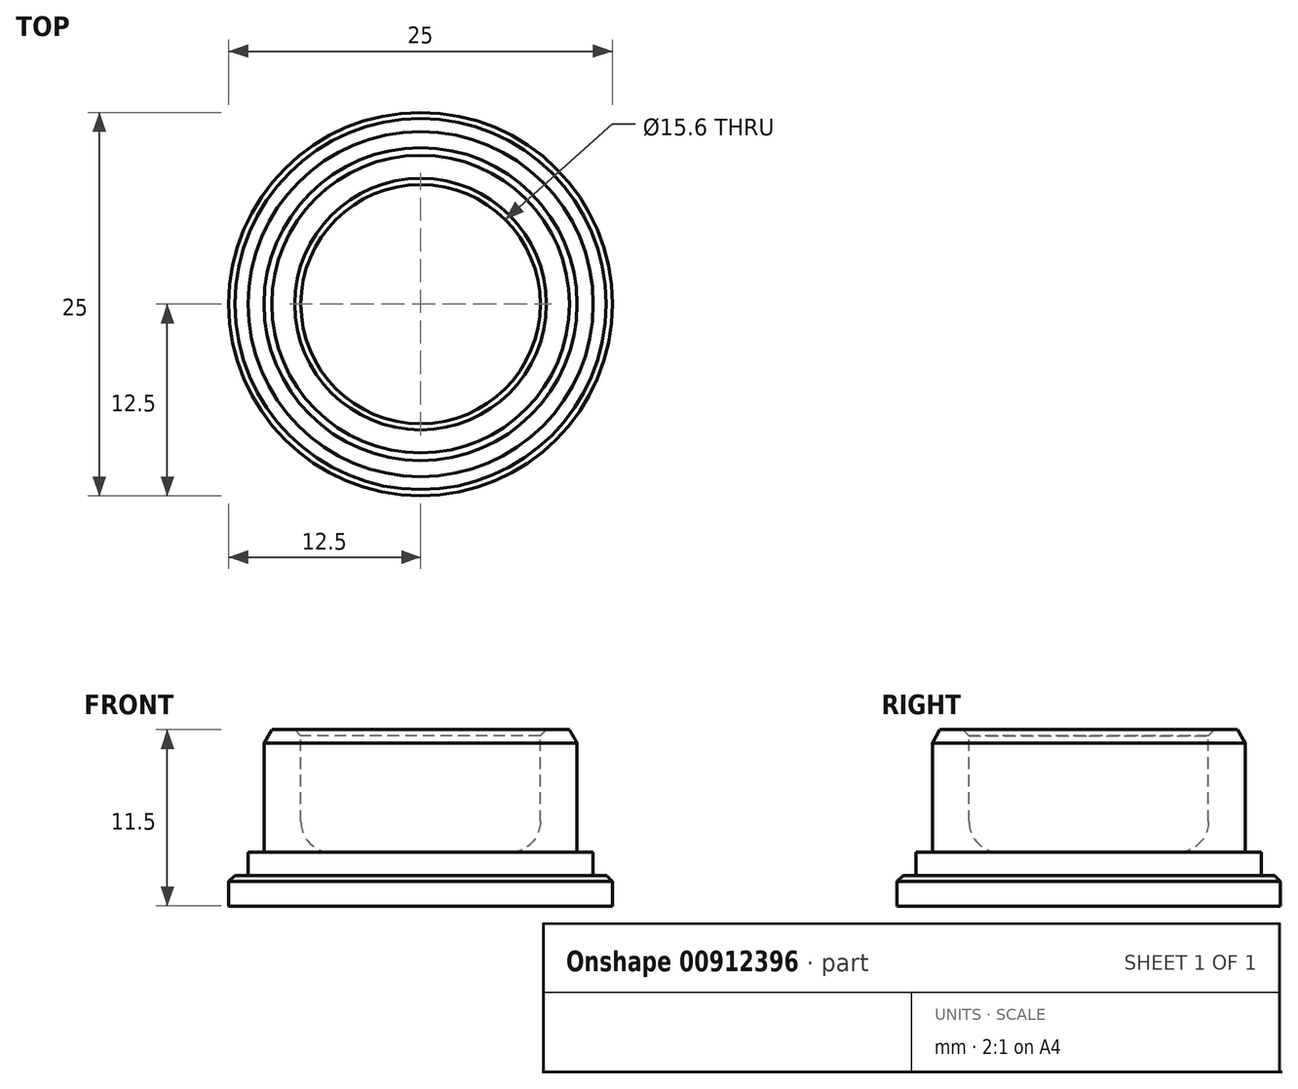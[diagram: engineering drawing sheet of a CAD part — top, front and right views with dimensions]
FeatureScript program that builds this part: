
annotation { "Feature Type Name" : "Feature", "Feature Type Description" : "" }
export const myFeature = defineFeature(function(context is Context, id is Id, definition is map)
    precondition{}
    {
        {
            var Q0;
            Q0=qCreatedBy(makeId("Front.planeOp"),FACE);
            var sketch = newSketch(context, id + "F0", { "sketchPlane" : qUnion([Q0])});
            skLineSegment(sketch, "E0", {"start": v(0, 14.43) * mm, "end": v(0, -11.95) * mm, "construction": true});
            skLineSegment(sketch, "E1", {"start": v(7.8, 5.82) * mm, "end": v(7.8, -2.18) * mm});
            skLineSegment(sketch, "E2", {"start": v(7.8, -2.18) * mm, "end": v(0, -2.18) * mm});
            skLineSegment(sketch, "E3", {"start": v(7.8, 5.82) * mm, "end": v(10.2, 5.82) * mm});
            skLineSegment(sketch, "E4", {"start": v(10.2, 5.82) * mm, "end": v(10.2, -2.18) * mm});
            skLineSegment(sketch, "E5", {"start": v(10.2, -2.18) * mm, "end": v(11.25, -2.18) * mm});
            skLineSegment(sketch, "E6", {"start": v(11.25, -2.18) * mm, "end": v(11.25, -3.68) * mm});
            skLineSegment(sketch, "E7", {"start": v(11.25, -3.68) * mm, "end": v(12.5, -3.68) * mm});
            skLineSegment(sketch, "E8", {"start": v(12.5, -3.68) * mm, "end": v(12.5, -5.68) * mm});
            skLineSegment(sketch, "E9", {"start": v(12.5, -5.68) * mm, "end": v(0, -5.68) * mm});
            skLineSegment(sketch, "E10", {"start": v(0, -2.18) * mm, "end": v(0, -5.68) * mm});
            skSolve(sketch);
        }
        {
            var Q0;
            Q0=makeQuery(id+"F0.imprint","IMPRINT",FACE,{"disambiguationData":[TD([[makeQuery(id+"F0.imprint","IMPRINT",EDGE,{"derivedFrom":sQuery(id+"F0.wireOp",EDGE,"E1")}),1.0]])]});
            var Q1;
            Q1=sQuery(id+"F0.wireOp",EDGE,"E0");
            revolve(context, id + "F1", {"surfaceOperationType" : NewSurfaceOperationType.NEW, "entities" : qUnion([Q0]), "axis" : qUnion([Q1]), "revolveType" : RevolveType.FULL});
        }
        {
            var Q0;
            Q0=makeQuery(id+"F1.opRevolve","SWEPT_EDGE",EDGE,{"disambiguationData":[OSD([sQuery(id+"F0.wireOp",EDGE,"E1"),sQuery(id+"F0.wireOp",EDGE,"E2")])]});
            fillet(context, id + "F2", {"entities" : qUnion([Q0]), "radius" : 2 * mm, "tangentPropagation" : true, "allowEdgeOverflow" : false});
        }
        {
            var Q0;
            Q0=makeQuery(id+"F1.opRevolve","SWEPT_EDGE",EDGE,{"disambiguationData":[OSD([sQuery(id+"F0.wireOp",EDGE,"E7"),sQuery(id+"F0.wireOp",EDGE,"E8")])]});
            chamfer(context, id + "F3", {"entities" : qUnion([Q0]), "width" : 0.4 * mm, "tangentPropagation" : true});
        }
        {
            var Q0;
            Q0=makeQuery(id+"F1.opRevolve","SWEPT_EDGE",EDGE,{"disambiguationData":[OSD([sQuery(id+"F0.wireOp",EDGE,"E3"),sQuery(id+"F0.wireOp",EDGE,"E4")])]});
            chamfer(context, id + "F4", {"entities" : qUnion([Q0]), "chamferType" : ChamferType.OFFSET_ANGLE, "width" : 0.5 * mm, "oppositeDirection" : false, "angle" : 60 * degree, "tangentPropagation" : true});
        }
        {
            var Q0;
            Q0=makeQuery(id+"F1.opRevolve","SWEPT_EDGE",EDGE,{"disambiguationData":[OSD([sQuery(id+"F0.wireOp",EDGE,"E1"),sQuery(id+"F0.wireOp",EDGE,"E3")])]});
            chamfer(context, id + "F5", {"entities" : qUnion([Q0]), "width" : 0.4 * mm, "tangentPropagation" : true});
        }
    });
